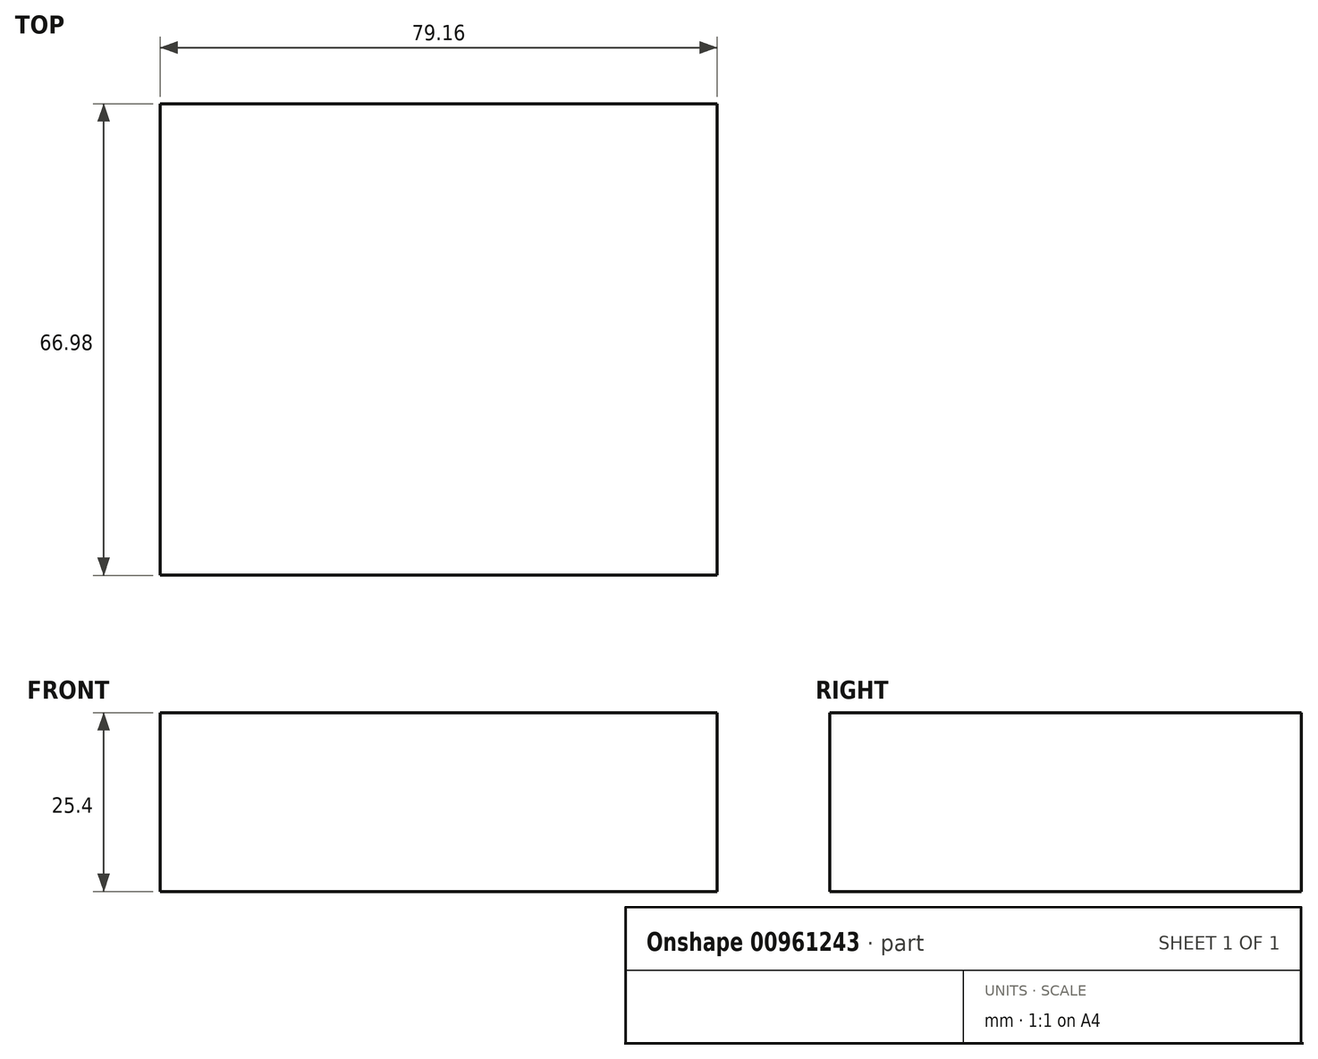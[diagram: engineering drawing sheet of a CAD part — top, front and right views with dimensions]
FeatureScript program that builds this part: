
annotation { "Feature Type Name" : "Feature", "Feature Type Description" : "" }
export const myFeature = defineFeature(function(context is Context, id is Id, definition is map)
    precondition{}
    {
        {
            var Q0;
            Q0=qCreatedBy(makeId("Top.planeOp"),FACE);
            var sketch = newSketch(context, id + "F0", { "sketchPlane" : qUnion([Q0])});
            skLineSegment(sketch, "E0.bottom", {"start": v(-53.85, -42.53) * mm, "end": v(25.3, -42.53) * mm});
            skLineSegment(sketch, "E0.top", {"start": v(-53.85, 24.45) * mm, "end": v(25.3, 24.45) * mm});
            skLineSegment(sketch, "E0.left", {"start": v(-53.85, -42.53) * mm, "end": v(-53.85, 24.45) * mm});
            skLineSegment(sketch, "E0.right", {"start": v(25.3, -42.53) * mm, "end": v(25.3, 24.45) * mm});
            skSolve(sketch);
        }
        {
            var Q0;
            Q0 = qSketchRegion(id + "F0", true);
            extrude(context, id + "F1", {"entities" : qUnion([Q0]), "depth" : 25.4 * mm, "offsetDistance" : 25.4 * mm});
        }
    });
